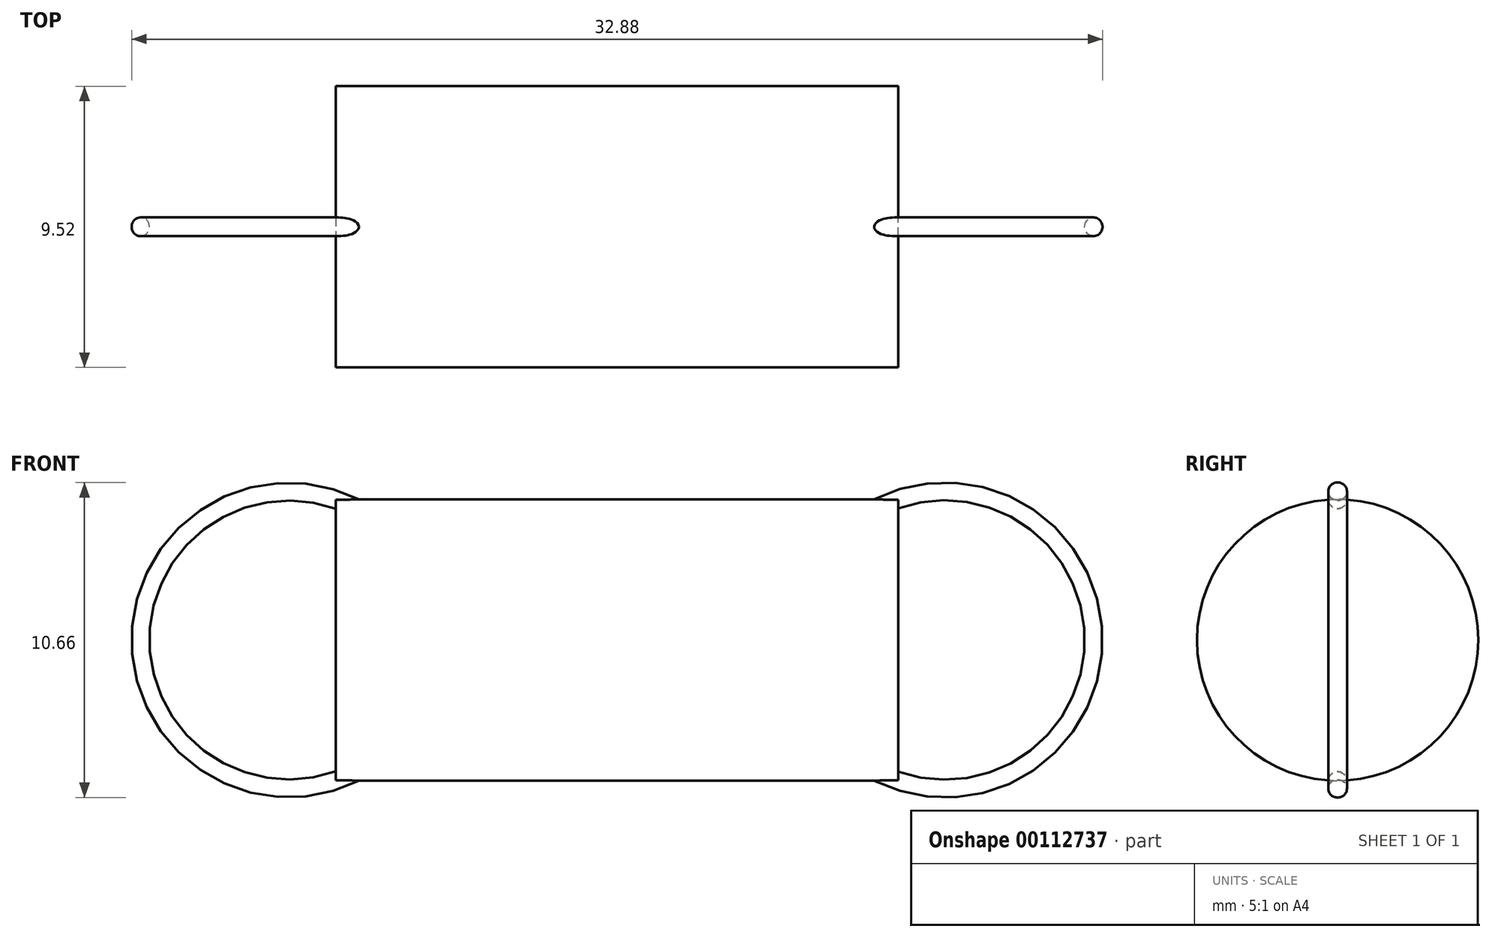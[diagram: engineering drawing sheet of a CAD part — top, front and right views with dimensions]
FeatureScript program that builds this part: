
annotation { "Feature Type Name" : "Feature", "Feature Type Description" : "" }
export const myFeature = defineFeature(function(context is Context, id is Id, definition is map)
    precondition{}
    {
        {
            var Q0;
            Q0=qCreatedBy(makeId("Front.planeOp"),FACE);
            var sketch = newSketch(context, id + "F0", { "sketchPlane" : qUnion([Q0])});
            skLineSegment(sketch, "E0", {"start": v(-9.53, 0) * mm, "end": v(9.53, 0) * mm});
            skLineSegment(sketch, "E1.bottom", {"start": v(-9.53, -4.76) * mm, "end": v(9.53, -4.76) * mm});
            skLineSegment(sketch, "E1.top", {"start": v(-9.53, 4.76) * mm, "end": v(9.52, 4.76) * mm});
            skLineSegment(sketch, "E1.left", {"start": v(-9.53, -4.76) * mm, "end": v(-9.53, 4.76) * mm});
            skLineSegment(sketch, "E1.right", {"start": v(9.53, -4.76) * mm, "end": v(9.52, 4.76) * mm});
            skPoint(sketch, "E1.middle", {"position": v(0, 0) * mm});
            skCircle(sketch, "E2", {"center": v(11.11, 0) * mm, "radius": 4.76 * mm});
            skLineSegment(sketch, "E3", {"start": v(0, 17.7) * mm, "end": v(0, -23.74) * mm, "construction": true});
            skCircle(sketch, "E4.MirrorC", {"center": v(-11.11, 0) * mm, "radius": 4.76 * mm});
            skSolve(sketch);
        }
        {
            var Q0;
            {var subQ1=sQuery(id+"F0.wireOp",EDGE,"E1.top");Q0=makeQuery(id+"F0.imprint","IMPRINT",FACE,{"disambiguationData":[TD([[makeQuery(id+"F0.imprint","IMPRINT",EDGE,{"derivedFrom":subQ1}),-1.0]])]});}
            var Q1;
            {var subQ0=sQuery(id+"F0.wireOp",EDGE,"E1.left");var subQ1=sQuery(id+"F0.wireOp",EDGE,"E0");var subQ2=makeQuery(id+"F0.imprint","INTERSECT",VERTEX,{"derivedFrom":[subQ1,subQ0]});Q1=makeQuery(id+"F0.imprint","IMPRINT",FACE,{"disambiguationData":[TD([[makeQuery(id+"F0.imprint","IMPRINT",EDGE,{"disambiguationData":[TD([[subQ2,-1.0]])],"derivedFrom":subQ1}),1.0]])]});}
            var Q2;
            {var subQ0=sQuery(id+"F0.wireOp",EDGE,"E1.right");var subQ1=sQuery(id+"F0.wireOp",EDGE,"E0");var subQ2=makeQuery(id+"F0.imprint","INTERSECT",VERTEX,{"derivedFrom":[subQ1,subQ0]});Q2=makeQuery(id+"F0.imprint","IMPRINT",FACE,{"disambiguationData":[TD([[makeQuery(id+"F0.imprint","IMPRINT",EDGE,{"disambiguationData":[TD([[subQ2,1.0]])],"derivedFrom":subQ1}),1.0]])]});}
            var Q3;
            Q3=sQuery(id+"F0.wireOp",EDGE,"E1.left");
            var Q4;
            Q4=sQuery(id+"F0.wireOp",EDGE,"E1.right");
            var Q5;
            Q5=sQuery(id+"F0.wireOp",EDGE,"E1.top");
            var Q6;
            Q6=sQuery(id+"F0.wireOp",EDGE,"E0");
            revolve(context, id + "F1", {"entities" : qUnion([Q0, Q1, Q2]), "surfaceEntities" : qUnion([Q3, Q4, Q5]), "axis" : qUnion([Q6]), "revolveType" : RevolveType.FULL});
        }
        {
            var Q0;
            Q0=makeQuery(id+"F1.opRevolve","SWEPT_FACE",FACE,{"disambiguationData":[OSD([sQuery(id+"F0.wireOp",EDGE,"E1.left")])]});
            cPlane(context, id + "F2", {"entities" : qUnion([Q0]), "cplaneType" : CPlaneType.OFFSET, "offset" : 0 * mm, "width" : 152.4 * mm, "height" : 152.4 * mm});
        }
        {
            var Q0;
            Q0=qCreatedBy(id+"F2.planeOp",FACE);
            var sketch = newSketch(context, id + "F3", { "sketchPlane" : qUnion([Q0])});
            skCircle(sketch, "E5", {"center": v(0, 4.76) * mm, "radius": 0.32 * mm});
            skSolve(sketch);
        }
        {
            var Q0;
            Q0=makeQuery(id+"F3.imprint","IMPRINT",FACE,{"disambiguationData":[TD([[makeQuery(id+"F3.imprint","IMPRINT",EDGE,{"derivedFrom":sQuery(id+"F3.wireOp",EDGE,"E5")}),1.0]])]});
            var Q1;
            Q1=sQuery(id+"F0.wireOp",EDGE,"E4.MirrorC");
            sweep(context, id + "F4", {"operationType" : NewBodyOperationType.ADD, "profiles" : qUnion([Q0]), "path" : qUnion([Q1])});
        }
        {
            var Q0;
            Q0=makeQuery(id+"F1.opRevolve","SWEPT_FACE",FACE,{"disambiguationData":[OSD([sQuery(id+"F0.wireOp",EDGE,"E1.right")])]});
            cPlane(context, id + "F5", {"entities" : qUnion([Q0]), "cplaneType" : CPlaneType.OFFSET, "offset" : 0 * mm, "width" : 152.4 * mm, "height" : 152.4 * mm});
        }
        {
            var Q0;
            Q0=qCreatedBy(id+"F5.planeOp",FACE);
            var sketch = newSketch(context, id + "F6", { "sketchPlane" : qUnion([Q0])});
            skCircle(sketch, "E6", {"center": v(0, 4.78) * mm, "radius": 0.32 * mm});
            skSolve(sketch);
        }
        {
            var Q0;
            Q0=makeQuery(id+"F6.imprint","IMPRINT",FACE,{"disambiguationData":[TD([[makeQuery(id+"F6.imprint","IMPRINT",EDGE,{"derivedFrom":sQuery(id+"F6.wireOp",EDGE,"E6")}),1.0]])]});
            var Q1;
            Q1=sQuery(id+"F0.wireOp",EDGE,"E2");
            revolve(context, id + "F7", {"operationType" : NewBodyOperationType.ADD, "entities" : qUnion([Q0]), "axis" : qUnion([Q1]), "revolveType" : RevolveType.FULL});
        }
    });
